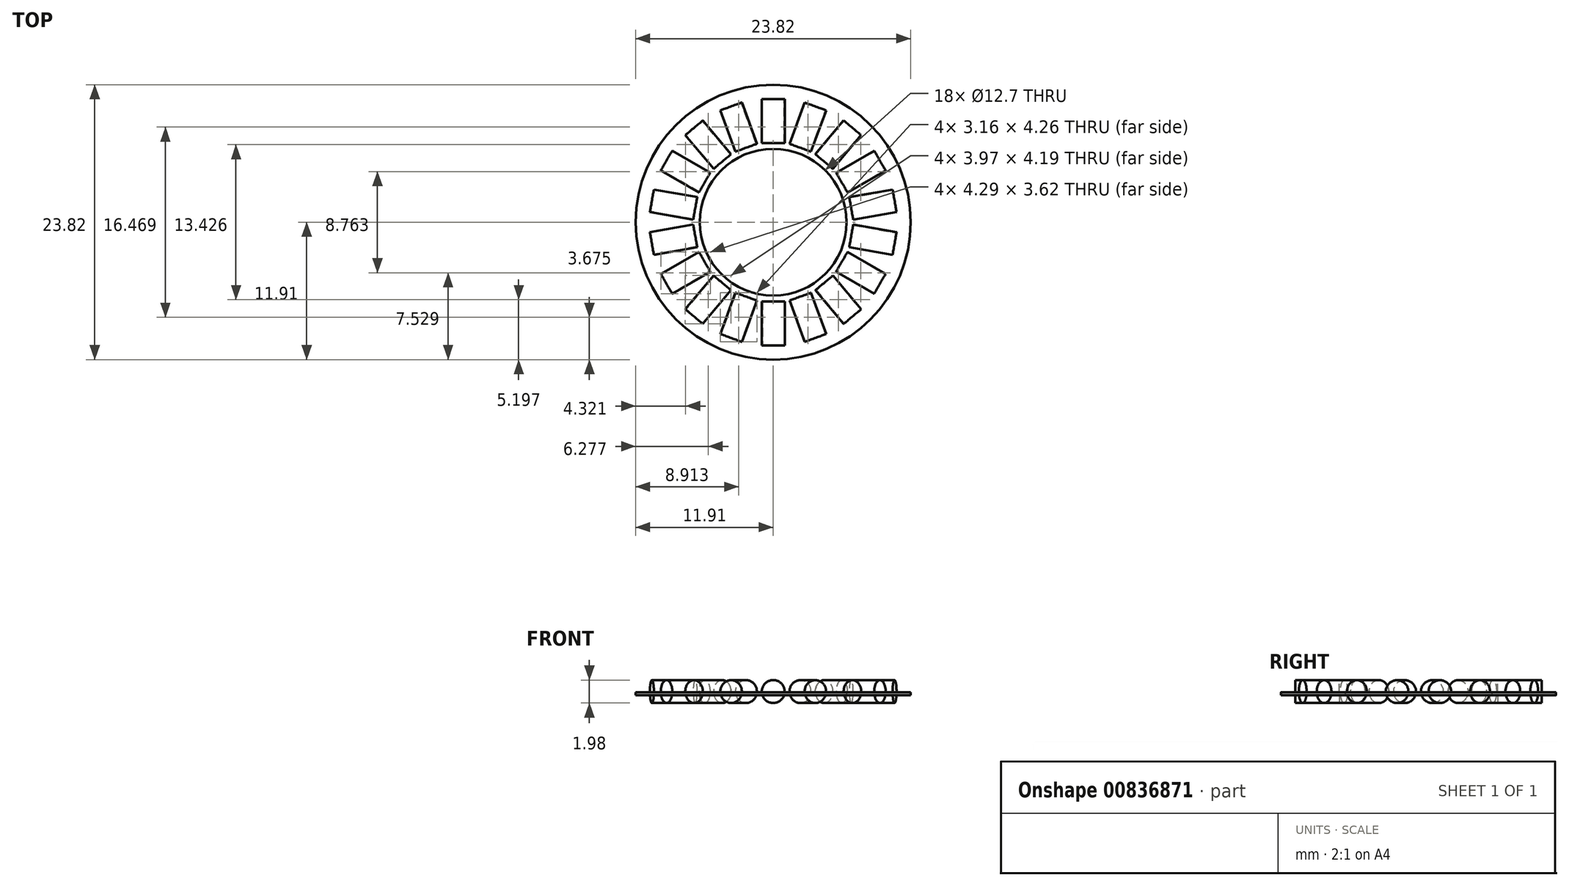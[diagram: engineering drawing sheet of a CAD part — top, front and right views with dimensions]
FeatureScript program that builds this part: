
annotation { "Feature Type Name" : "Feature", "Feature Type Description" : "" }
export const myFeature = defineFeature(function(context is Context, id is Id, definition is map)
    precondition{}
    {
        {
            var Q0;
            Q0=qCreatedBy(makeId("Top.planeOp"),FACE);
            var sketch = newSketch(context, id + "F0", { "sketchPlane" : qUnion([Q0])});
            skCircle(sketch, "E0", {"center": v(0, 0) * mm, "radius": 11.9 * mm});
            skCircle(sketch, "E1", {"center": v(0, 0) * mm, "radius": 6.35 * mm});
            skSolve(sketch);
        }
        {
            var Q0;
            Q0 = qSketchRegion(id + "F0", true);
            extrude(context, id + "F1", {"entities" : qUnion([Q0]), "depth" : 0.25 * mm, "offsetDistance" : 25.4 * mm, "symmetric" : true});
        }
        {
            var Q0;
            Q0=qCreatedBy(makeId("Front.planeOp"),FACE);
            cPlane(context, id + "F2", {"entities" : qUnion([Q0]), "cplaneType" : CPlaneType.OFFSET, "offset" : 10.67 * mm, "width" : 152.4 * mm, "height" : 152.4 * mm});
        }
        {
            var Q0;
            Q0=qCreatedBy(id+"F2.planeOp",FACE);
            var sketch = newSketch(context, id + "F3", { "sketchPlane" : qUnion([Q0])});
            skCircle(sketch, "E2", {"center": v(0, 0.2) * mm, "radius": 1 * mm});
            skSolve(sketch);
        }
        {
            var Q0;
            Q0 = qSketchRegion(id + "F3", true);
            extrude(context, id + "F4", {"entities" : qUnion([Q0]), "operationType" : NewBodyOperationType.ADD, "oppositeDirection" : true, "depth" : 3.8 * mm, "offsetDistance" : 25.4 * mm});
        }
        {
            var Q0;
            Q0=makeQuery(id+"F1.opExtrude","SWEPT_BODY",BODY,{"disambiguationData":[OSD([sQuery(id+"F0.wireOp",EDGE,"E0"),sQuery(id+"F0.wireOp",EDGE,"E1")])]});
            var Q1;
            Q1=makeQuery(id+"F1.opExtrude","SWEPT_FACE",FACE,{"disambiguationData":[OSD([sQuery(id+"F0.wireOp",EDGE,"E1")])]});
            circularPattern(context, id + "F5", {"entities" : qUnion([Q0]), "axis" : qUnion([Q1]), "angle" : 360 * degree, "instanceCount" : 18, "equalSpace" : true});
        }
    });
